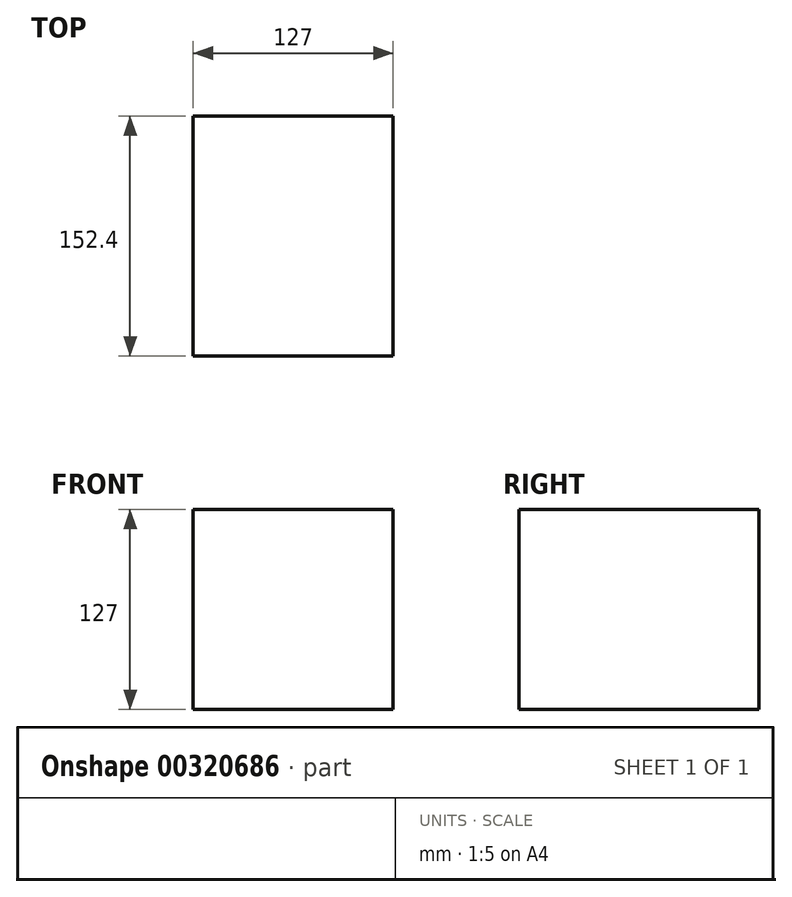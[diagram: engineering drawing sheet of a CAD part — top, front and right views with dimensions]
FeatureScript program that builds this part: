
annotation { "Feature Type Name" : "Feature", "Feature Type Description" : "" }
export const myFeature = defineFeature(function(context is Context, id is Id, definition is map)
    precondition{}
    {
        {
            var Q0;
            Q0=qCreatedBy(makeId("Front.planeOp"),FACE);
            var sketch = newSketch(context, id + "F0", { "sketchPlane" : qUnion([Q0])});
            skLineSegment(sketch, "E0.bottom", {"start": v(-38.46, -44.53) * mm, "end": v(88.54, -44.53) * mm});
            skLineSegment(sketch, "E0.top", {"start": v(-38.46, 82.47) * mm, "end": v(88.54, 82.47) * mm});
            skLineSegment(sketch, "E0.left", {"start": v(-38.46, -44.53) * mm, "end": v(-38.46, 82.47) * mm});
            skLineSegment(sketch, "E0.right", {"start": v(88.54, -44.53) * mm, "end": v(88.54, 82.47) * mm});
            skPoint(sketch, "E0.middle", {"position": v(25.04, 18.97) * mm});
            skSolve(sketch);
        }
        {
            var Q0;
            Q0=makeQuery(id+"F0.imprint","IMPRINT",FACE,{"disambiguationData":[TD([[makeQuery(id+"F0.imprint","IMPRINT",EDGE,{"derivedFrom":sQuery(id+"F0.wireOp",EDGE,"E0.bottom")}),1.0]])]});
            extrude(context, id + "F1", {"entities" : qUnion([Q0]), "depth" : 25.4 * mm});
        }
        {
            var Q0;
            Q0=makeQuery(id+"F1.opExtrude","CAP_FACE",FACE,{"disambiguationData":[OSD([sQuery(id+"F0.wireOp",EDGE,"E0.bottom"),sQuery(id+"F0.wireOp",EDGE,"E0.top"),sQuery(id+"F0.wireOp",EDGE,"E0.left"),sQuery(id+"F0.wireOp",EDGE,"E0.right")])],"isStart":false});
            extrude(context, id + "F2", {"entities" : qUnion([Q0]), "operationType" : NewBodyOperationType.ADD, "depth" : 101.6 * mm});
        }
        {
            var Q0;
            Q0=makeQuery(id+"F2.opExtrude","CAP_FACE",FACE,{"disambiguationData":[OSD([sQuery(id+"F0.wireOp",EDGE,"E0.bottom"),sQuery(id+"F0.wireOp",EDGE,"E0.top"),sQuery(id+"F0.wireOp",EDGE,"E0.left"),sQuery(id+"F0.wireOp",EDGE,"E0.right")])],"isStart":false});
            var sketch = newSketch(context, id + "F3", { "sketchPlane" : qUnion([Q0])});
            skSolve(sketch);
        }
        {
            var Q0;
            Q0=makeQuery(id+"F3.imprint","IMPRINT",FACE,{"disambiguationData":[TD([[makeQuery(id+"F3.imprint","IMPRINT",EDGE,{"derivedFrom":makeQuery(id+"F2.opExtrude","CAP_EDGE",EDGE,{"disambiguationData":[OSD([sQuery(id+"F0.wireOp",EDGE,"E0.bottom")])],"isStart":false})}),1.0]])]});
            extrude(context, id + "F4", {"entities" : qUnion([Q0]), "operationType" : NewBodyOperationType.ADD, "depth" : 25.4 * mm});
        }
    });
